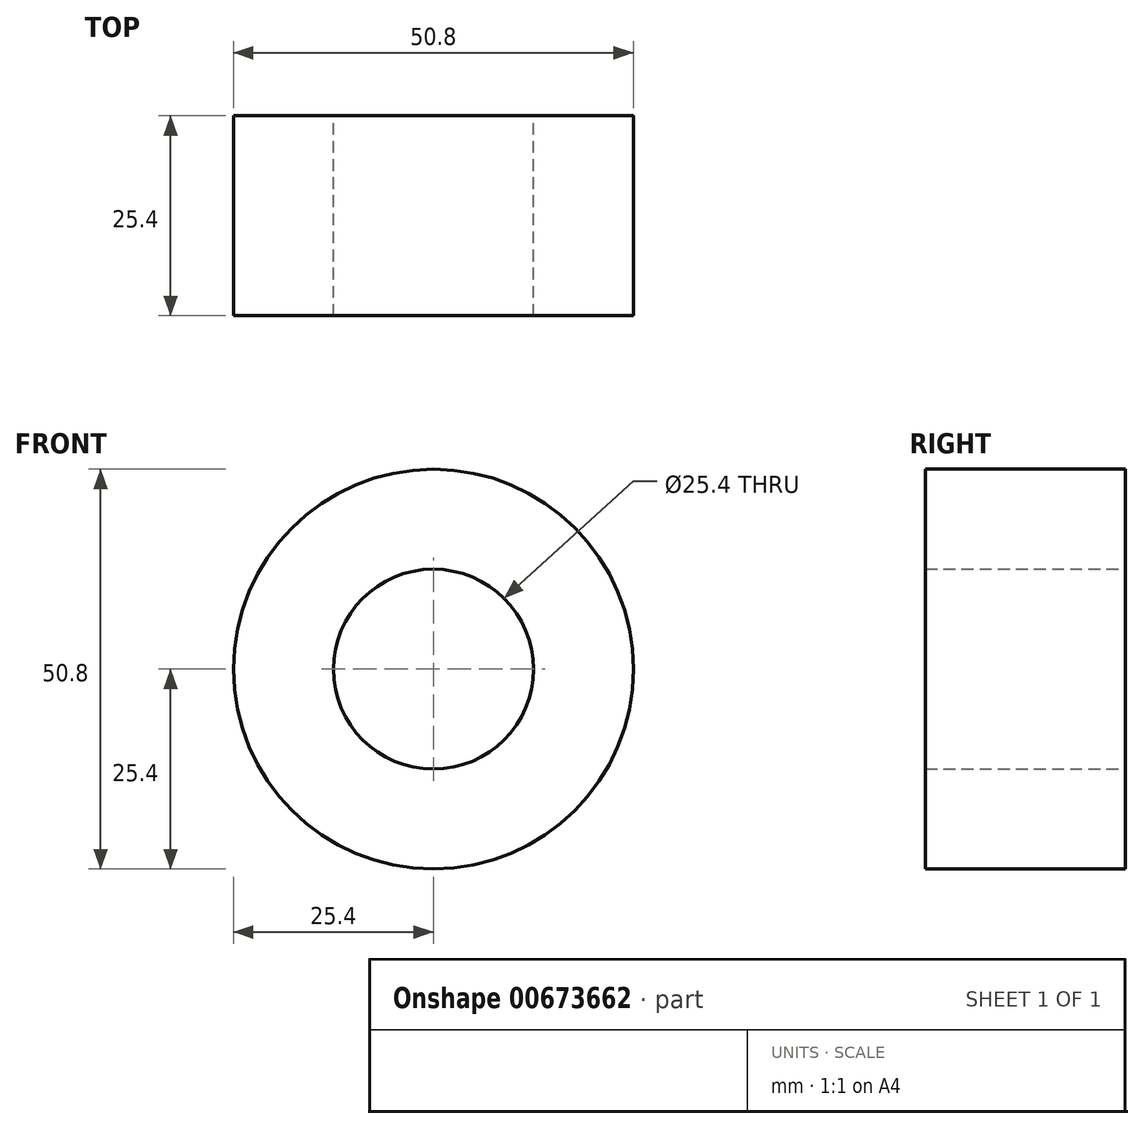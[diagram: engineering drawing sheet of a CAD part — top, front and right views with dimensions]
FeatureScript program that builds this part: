
annotation { "Feature Type Name" : "Feature", "Feature Type Description" : "" }
export const myFeature = defineFeature(function(context is Context, id is Id, definition is map)
    precondition{}
    {
        {
            var Q0;
            Q0=qCreatedBy(makeId("Front.planeOp"),FACE);
            var sketch = newSketch(context, id + "F0", { "sketchPlane" : qUnion([Q0])});
            skCircle(sketch, "E0", {"center": v(0, 0) * mm, "radius": 25.4 * mm});
            skCircle(sketch, "E1", {"center": v(0, 0) * mm, "radius": 12.7 * mm});
            skSolve(sketch);
        }
        {
            var Q0;
            Q0 = qSketchRegion(id + "F0", true);
            extrude(context, id + "F1", {"entities" : qUnion([Q0]), "endBound" : BoundingType.SYMMETRIC, "depth" : 25.4 * mm, "offsetDistance" : 25.4 * mm});
        }
    });
